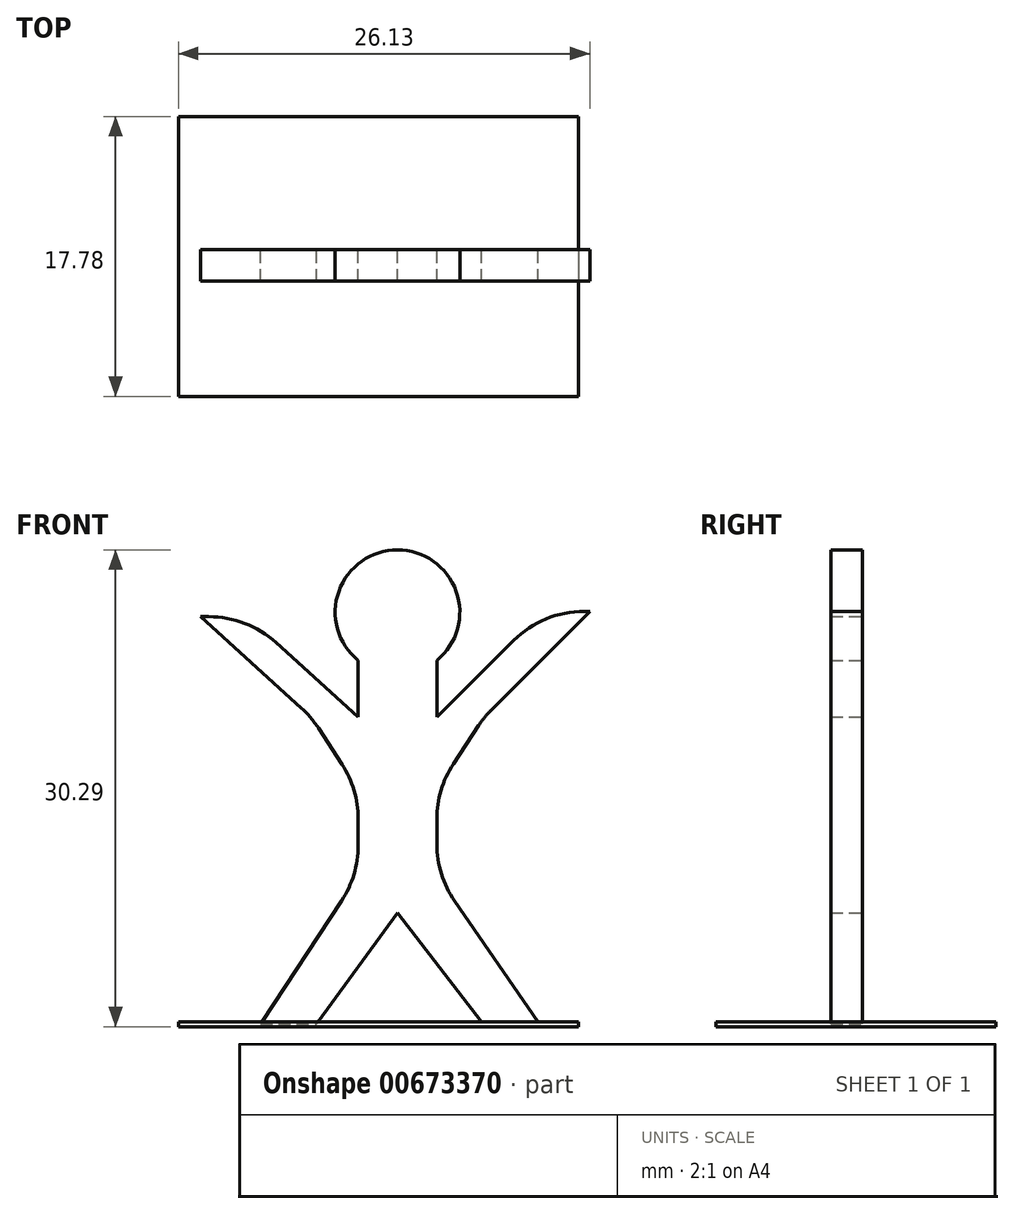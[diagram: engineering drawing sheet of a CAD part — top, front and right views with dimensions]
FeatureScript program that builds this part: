
annotation { "Feature Type Name" : "Feature", "Feature Type Description" : "" }
export const myFeature = defineFeature(function(context is Context, id is Id, definition is map)
    precondition{}
    {
        {
            var Q0;
            Q0=qCreatedBy(makeId("Top.planeOp"),FACE);
            var sketch = newSketch(context, id + "F0", { "sketchPlane" : qUnion([Q0])});
            skLineSegment(sketch, "E0", {"start": v(-35.92, 17.1) * mm, "end": v(-10.52, 17.1) * mm});
            skLineSegment(sketch, "E1", {"start": v(-10.52, 17.1) * mm, "end": v(-10.52, -0.68) * mm});
            skLineSegment(sketch, "E2", {"start": v(-10.52, -0.68) * mm, "end": v(-35.92, -0.68) * mm});
            skLineSegment(sketch, "E3", {"start": v(-35.92, -0.68) * mm, "end": v(-35.92, 17.1) * mm});
            skSolve(sketch);
        }
        {
            var Q0;
            Q0=makeQuery(id+"F0.imprint","IMPRINT",FACE,{"disambiguationData":[TD([[makeQuery(id+"F0.imprint","IMPRINT",EDGE,{"derivedFrom":sQuery(id+"F0.wireOp",EDGE,"E0")}),-1.0]])]});
            extrude(context, id + "F1", {"entities" : qUnion([Q0]), "depth" : 0.3 * mm, "offsetDistance" : 25.4 * mm});
        }
        {
            var Q0;
            Q0=qCreatedBy(makeId("Front.planeOp"),FACE);
            var sketch = newSketch(context, id + "F2", { "sketchPlane" : qUnion([Q0])});
            skLineSegment(sketch, "E4", {"start": v(-36.95, 30.73) * mm, "end": v(-36.95, 27.13) * mm});
            skLineSegment(sketch, "E5", {"start": v(-31.95, 30.73) * mm, "end": v(-31.95, 27.13) * mm});
            skLineSegment(sketch, "E6", {"start": v(-31.95, 27.13) * mm, "end": v(-27.07, 32) * mm});
            skLineSegment(sketch, "E7", {"start": v(-22.6, 33.84) * mm, "end": v(-22.23, 33.84) * mm});
            skLineSegment(sketch, "E8", {"start": v(-22.23, 33.84) * mm, "end": v(-28.49, 27.59) * mm});
            skLineSegment(sketch, "E9", {"start": v(-29.3, 26.59) * mm, "end": v(-30.9, 24.15) * mm});
            skLineSegment(sketch, "E10", {"start": v(-31.95, 20.66) * mm, "end": v(-31.95, 19.05) * mm});
            skLineSegment(sketch, "E11", {"start": v(-30.83, 15.45) * mm, "end": v(-25.54, 7.77) * mm});
            skLineSegment(sketch, "E12", {"start": v(-25.54, 7.77) * mm, "end": v(-29.12, 7.77) * mm});
            skLineSegment(sketch, "E13", {"start": v(-29.12, 7.77) * mm, "end": v(-34.45, 14.7) * mm});
            skLineSegment(sketch, "E14", {"start": v(-36.95, 27.13) * mm, "end": v(-42.18, 31.86) * mm});
            skLineSegment(sketch, "E15", {"start": v(-46.44, 33.5) * mm, "end": v(-46.97, 33.5) * mm});
            skLineSegment(sketch, "E16", {"start": v(-46.97, 33.5) * mm, "end": v(-40.54, 27.69) * mm});
            skLineSegment(sketch, "E17", {"start": v(-39.47, 26.44) * mm, "end": v(-37.97, 24.13) * mm});
            skLineSegment(sketch, "E18", {"start": v(-36.95, 20.67) * mm, "end": v(-36.95, 18.96) * mm});
            skLineSegment(sketch, "E19", {"start": v(-38, 15.47) * mm, "end": v(-43.15, 7.64) * mm});
            skLineSegment(sketch, "E20", {"start": v(-43.15, 7.64) * mm, "end": v(-39.58, 7.64) * mm});
            skLineSegment(sketch, "E21", {"start": v(-39.58, 7.64) * mm, "end": v(-34.45, 14.7) * mm});
            skPoint(sketch, "E22.visualSharp", {"position": v(-25.22, 33.84) * mm});
            skArc(sketch, "E22.filletArc", {"start": v(-22.6, 33.84) * mm, "mid": v(-25.02, 33.36) * mm, "end": v(-27.07, 32) * mm});
            skPoint(sketch, "E23.visualSharp", {"position": v(-44, 33.5) * mm});
            skArc(sketch, "E23.filletArc", {"start": v(-42.18, 31.86) * mm, "mid": v(-44.16, 33.08) * mm, "end": v(-46.44, 33.5) * mm});
            skPoint(sketch, "E24.visualSharp", {"position": v(-39.92, 27.13) * mm});
            skArc(sketch, "E24.filletArc", {"start": v(-39.47, 26.44) * mm, "mid": v(-39.96, 27.1) * mm, "end": v(-40.54, 27.69) * mm});
            skPoint(sketch, "E25.visualSharp", {"position": v(-36.95, 22.55) * mm});
            skArc(sketch, "E25.filletArc", {"start": v(-36.95, 20.67) * mm, "mid": v(-37.21, 22.47) * mm, "end": v(-37.97, 24.13) * mm});
            skPoint(sketch, "E26.visualSharp", {"position": v(-31.95, 22.56) * mm});
            skArc(sketch, "E26.filletArc", {"start": v(-30.9, 24.15) * mm, "mid": v(-31.69, 22.48) * mm, "end": v(-31.95, 20.66) * mm});
            skPoint(sketch, "E27.visualSharp", {"position": v(-28.95, 27.13) * mm});
            skArc(sketch, "E27.filletArc", {"start": v(-28.49, 27.59) * mm, "mid": v(-28.92, 27.11) * mm, "end": v(-29.3, 26.59) * mm});
            skPoint(sketch, "E28.visualSharp", {"position": v(-31.95, 17.08) * mm});
            skArc(sketch, "E28.filletArc", {"start": v(-31.95, 19.05) * mm, "mid": v(-31.67, 17.16) * mm, "end": v(-30.83, 15.45) * mm});
            skPoint(sketch, "E29.visualSharp", {"position": v(-36.95, 17.06) * mm});
            skArc(sketch, "E29.filletArc", {"start": v(-38, 15.47) * mm, "mid": v(-37.22, 17.14) * mm, "end": v(-36.95, 18.96) * mm});
            skCircle(sketch, "E30", {"center": v(-34.45, 33.8) * mm, "radius": 3.96 * mm});
            skSolve(sketch);
        }
        {
            var Q0;
            {var subQ0=sQuery(id+"F2.wireOp",EDGE,"E30");var subQ1=makeQuery(id+"F2.imprint","INTERSECT",VERTEX,{"derivedFrom":[sQuery(id+"F2.wireOp",EDGE,"E4"),subQ0]});Q0=makeQuery(id+"F2.imprint","IMPRINT",FACE,{"disambiguationData":[TD([[makeQuery(id+"F2.imprint","IMPRINT",EDGE,{"disambiguationData":[TD([[subQ1,-1.0]])],"derivedFrom":subQ0}),1.0]])]});}
            var Q1;
            {var subQ1=sQuery(id+"F2.wireOp",EDGE,"E4");Q1=makeQuery(id+"F2.imprint","IMPRINT",FACE,{"disambiguationData":[TD([[makeQuery(id+"F2.imprint","IMPRINT",EDGE,{"derivedFrom":subQ1}),1.0]])]});}
            extrude(context, id + "F3", {"entities" : qUnion([Q0, Q1]), "depth" : 2 * mm, "offsetDistance" : 25.4 * mm});
        }
        {
            var Q0;
            Q0=makeQuery(id+"F3.opExtrude","SWEPT_BODY",BODY,{"disambiguationData":[OSD([sQuery(id+"F2.wireOp",EDGE,"E4"),sQuery(id+"F2.wireOp",EDGE,"E5"),sQuery(id+"F2.wireOp",EDGE,"E6"),sQuery(id+"F2.wireOp",EDGE,"E7"),sQuery(id+"F2.wireOp",EDGE,"E8"),sQuery(id+"F2.wireOp",EDGE,"E9"),sQuery(id+"F2.wireOp",EDGE,"E10"),sQuery(id+"F2.wireOp",EDGE,"E11"),sQuery(id+"F2.wireOp",EDGE,"E12"),sQuery(id+"F2.wireOp",EDGE,"E13"),sQuery(id+"F2.wireOp",EDGE,"E14"),sQuery(id+"F2.wireOp",EDGE,"E15"),sQuery(id+"F2.wireOp",EDGE,"E16"),sQuery(id+"F2.wireOp",EDGE,"E17"),sQuery(id+"F2.wireOp",EDGE,"E18"),sQuery(id+"F2.wireOp",EDGE,"E19"),sQuery(id+"F2.wireOp",EDGE,"E20"),sQuery(id+"F2.wireOp",EDGE,"E21"),sQuery(id+"F2.wireOp",EDGE,"E22.filletArc"),sQuery(id+"F2.wireOp",EDGE,"E23.filletArc"),sQuery(id+"F2.wireOp",EDGE,"E24.filletArc"),sQuery(id+"F2.wireOp",EDGE,"E25.filletArc"),sQuery(id+"F2.wireOp",EDGE,"E26.filletArc"),sQuery(id+"F2.wireOp",EDGE,"E27.filletArc"),sQuery(id+"F2.wireOp",EDGE,"E28.filletArc"),sQuery(id+"F2.wireOp",EDGE,"E29.filletArc"),sQuery(id+"F2.wireOp",EDGE,"E30")])]});
            transform(context, id + "F4", {"entities" : qUnion([Q0]), "transformType" : TransformType.TRANSLATION_3D, "dx" : 20.07 * mm, "dy" : 0 * mm, "dz" : 0 * mm, "makeCopy" : false});
        }
        {
            var Q0;
            Q0=makeQuery(id+"F3.opExtrude","SWEPT_BODY",BODY,{"disambiguationData":[OSD([sQuery(id+"F2.wireOp",EDGE,"E4"),sQuery(id+"F2.wireOp",EDGE,"E5"),sQuery(id+"F2.wireOp",EDGE,"E6"),sQuery(id+"F2.wireOp",EDGE,"E7"),sQuery(id+"F2.wireOp",EDGE,"E8"),sQuery(id+"F2.wireOp",EDGE,"E9"),sQuery(id+"F2.wireOp",EDGE,"E10"),sQuery(id+"F2.wireOp",EDGE,"E11"),sQuery(id+"F2.wireOp",EDGE,"E12"),sQuery(id+"F2.wireOp",EDGE,"E13"),sQuery(id+"F2.wireOp",EDGE,"E14"),sQuery(id+"F2.wireOp",EDGE,"E15"),sQuery(id+"F2.wireOp",EDGE,"E16"),sQuery(id+"F2.wireOp",EDGE,"E17"),sQuery(id+"F2.wireOp",EDGE,"E18"),sQuery(id+"F2.wireOp",EDGE,"E19"),sQuery(id+"F2.wireOp",EDGE,"E20"),sQuery(id+"F2.wireOp",EDGE,"E21"),sQuery(id+"F2.wireOp",EDGE,"E22.filletArc"),sQuery(id+"F2.wireOp",EDGE,"E23.filletArc"),sQuery(id+"F2.wireOp",EDGE,"E24.filletArc"),sQuery(id+"F2.wireOp",EDGE,"E25.filletArc"),sQuery(id+"F2.wireOp",EDGE,"E26.filletArc"),sQuery(id+"F2.wireOp",EDGE,"E27.filletArc"),sQuery(id+"F2.wireOp",EDGE,"E28.filletArc"),sQuery(id+"F2.wireOp",EDGE,"E29.filletArc"),sQuery(id+"F2.wireOp",EDGE,"E30")])]});
            transform(context, id + "F5", {"entities" : qUnion([Q0]), "transformType" : TransformType.TRANSLATION_3D, "dx" : -7.62 * mm, "dy" : 8.64 * mm, "dz" : -7.47 * mm, "makeCopy" : false});
        }
    });
